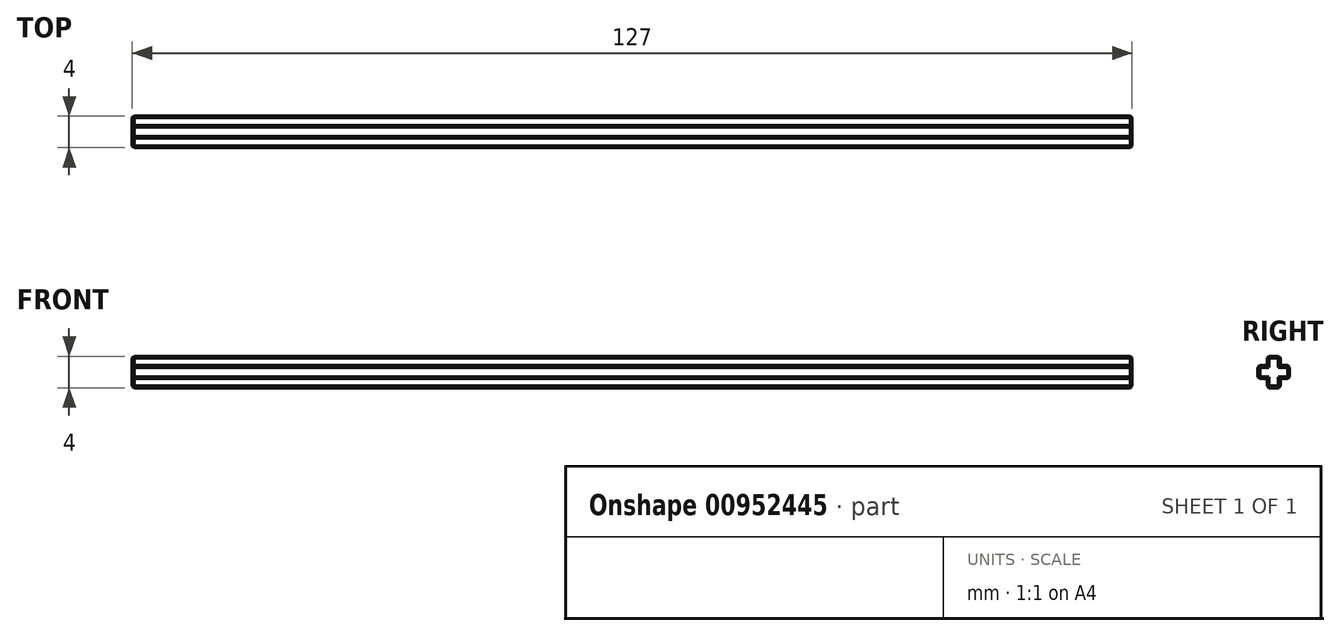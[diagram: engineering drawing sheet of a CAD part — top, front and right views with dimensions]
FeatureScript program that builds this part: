
annotation { "Feature Type Name" : "Feature", "Feature Type Description" : "" }
export const myFeature = defineFeature(function(context is Context, id is Id, definition is map)
    precondition{}
    {
        {
            var Q0;
            Q0=qCreatedBy(makeId("Right.planeOp"),FACE);
            var sketch = newSketch(context, id + "F0", { "sketchPlane" : qUnion([Q0])});
            skLineSegment(sketch, "E0.bottom", {"start": v(0.8, 2) * mm, "end": v(-0.8, 2) * mm});
            skLineSegment(sketch, "E0.top", {"start": v(0.8, -2) * mm, "end": v(-0.8, -2) * mm});
            skLineSegment(sketch, "E0.left", {"start": v(0.8, 2) * mm, "end": v(0.8, -2) * mm});
            skLineSegment(sketch, "E0.right", {"start": v(-0.8, 2) * mm, "end": v(-0.8, -2) * mm});
            skPoint(sketch, "E0.middle", {"position": v(0, 0) * mm});
            skLineSegment(sketch, "E1.bottom", {"start": v(-2, -0.8) * mm, "end": v(2, -0.8) * mm});
            skLineSegment(sketch, "E1.top", {"start": v(-2, 0.8) * mm, "end": v(2, 0.8) * mm});
            skLineSegment(sketch, "E1.left", {"start": v(-2, -0.8) * mm, "end": v(-2, 0.8) * mm});
            skLineSegment(sketch, "E1.right", {"start": v(2, -0.8) * mm, "end": v(2, 0.8) * mm});
            skSolve(sketch);
        }
        {
            var Q0;
            {var subQ5=sQuery(id+"F0.wireOp",EDGE,"E1.left");Q0=makeQuery(id+"F0.imprint","IMPRINT",FACE,{"disambiguationData":[TD([[makeQuery(id+"F0.imprint","IMPRINT",EDGE,{"derivedFrom":subQ5}),-1.0]])]});}
            var Q1;
            {var subQ0=sQuery(id+"F0.wireOp",EDGE,"E1.top");var subQ1=sQuery(id+"F0.wireOp",EDGE,"E0.left");var subQ2=makeQuery(id+"F0.imprint","INTERSECT",VERTEX,{"derivedFrom":[subQ1,subQ0]});Q1=makeQuery(id+"F0.imprint","IMPRINT",FACE,{"disambiguationData":[TD([[makeQuery(id+"F0.imprint","IMPRINT",EDGE,{"disambiguationData":[TD([[subQ2,-1.0]])],"derivedFrom":subQ1}),-1.0]])]});}
            var Q2;
            {var subQ0=sQuery(id+"F0.wireOp",EDGE,"E0.top");Q2=makeQuery(id+"F0.imprint","IMPRINT",FACE,{"disambiguationData":[TD([[makeQuery(id+"F0.imprint","IMPRINT",EDGE,{"derivedFrom":subQ0}),-1.0]])]});}
            var Q3;
            {var subQ5=sQuery(id+"F0.wireOp",EDGE,"E1.right");Q3=makeQuery(id+"F0.imprint","IMPRINT",FACE,{"disambiguationData":[TD([[makeQuery(id+"F0.imprint","IMPRINT",EDGE,{"derivedFrom":subQ5}),1.0]])]});}
            var Q4;
            {var subQ0=sQuery(id+"F0.wireOp",EDGE,"E0.bottom");Q4=makeQuery(id+"F0.imprint","IMPRINT",FACE,{"disambiguationData":[TD([[makeQuery(id+"F0.imprint","IMPRINT",EDGE,{"derivedFrom":subQ0}),1.0]])]});}
            extrude(context, id + "F1", {"entities" : qUnion([Q0, Q1, Q2, Q3, Q4]), "depth" : 127 * mm, "offsetDistance" : 25.4 * mm});
        }
        {
            var Q0;
            Q0=makeQuery(id+"F1.opExtrude","SWEPT_EDGE",EDGE,{"disambiguationData":[OSD([sQuery(id+"F0.wireOp",EDGE,"ookbRjFh-wDmi-CqYK-rmM9-PLN8MNht7uDI"),sQuery(id+"F0.wireOp",EDGE,"E1.bottom"),sQuery(id+"F0.wireOp",EDGE,"E1.left")])]});
            var Q1;
            Q1=makeQuery(id+"F1.opExtrude","SWEPT_EDGE",EDGE,{"disambiguationData":[OSD([sQuery(id+"F0.wireOp",EDGE,"ookbRjFh-wDmi-CqYK-rmM9-PLN8MNht7uDI"),sQuery(id+"F0.wireOp",EDGE,"E1.top"),sQuery(id+"F0.wireOp",EDGE,"E1.left")])]});
            var Q2;
            Q2=makeQuery(id+"F1.opExtrude","SWEPT_EDGE",EDGE,{"disambiguationData":[OSD([sQuery(id+"F0.wireOp",EDGE,"ookbRjFh-wDmi-CqYK-rmM9-PLN8MNht7uDI"),sQuery(id+"F0.wireOp",EDGE,"E0.bottom"),sQuery(id+"F0.wireOp",EDGE,"E0.right")])]});
            var Q3;
            Q3=makeQuery(id+"F1.opExtrude","SWEPT_EDGE",EDGE,{"disambiguationData":[OSD([sQuery(id+"F0.wireOp",EDGE,"ookbRjFh-wDmi-CqYK-rmM9-PLN8MNht7uDI"),sQuery(id+"F0.wireOp",EDGE,"E0.top"),sQuery(id+"F0.wireOp",EDGE,"E0.right")])]});
            var Q4;
            Q4=makeQuery(id+"F1.opExtrude","SWEPT_EDGE",EDGE,{"disambiguationData":[OSD([sQuery(id+"F0.wireOp",EDGE,"ookbRjFh-wDmi-CqYK-rmM9-PLN8MNht7uDI"),sQuery(id+"F0.wireOp",EDGE,"E0.top"),sQuery(id+"F0.wireOp",EDGE,"E0.left")])]});
            var Q5;
            Q5=makeQuery(id+"F1.opExtrude","SWEPT_EDGE",EDGE,{"disambiguationData":[OSD([sQuery(id+"F0.wireOp",EDGE,"ookbRjFh-wDmi-CqYK-rmM9-PLN8MNht7uDI"),sQuery(id+"F0.wireOp",EDGE,"E1.bottom"),sQuery(id+"F0.wireOp",EDGE,"E1.right")])]});
            var Q6;
            Q6=makeQuery(id+"F1.opExtrude","SWEPT_EDGE",EDGE,{"disambiguationData":[OSD([sQuery(id+"F0.wireOp",EDGE,"ookbRjFh-wDmi-CqYK-rmM9-PLN8MNht7uDI"),sQuery(id+"F0.wireOp",EDGE,"E1.top"),sQuery(id+"F0.wireOp",EDGE,"E1.right")])]});
            var Q7;
            Q7=makeQuery(id+"F1.opExtrude","SWEPT_EDGE",EDGE,{"disambiguationData":[OSD([sQuery(id+"F0.wireOp",EDGE,"ookbRjFh-wDmi-CqYK-rmM9-PLN8MNht7uDI"),sQuery(id+"F0.wireOp",EDGE,"E0.bottom"),sQuery(id+"F0.wireOp",EDGE,"E0.left")])]});
            var Q8;
            {var subQ0=sQuery(id+"F0.wireOp",EDGE,"E1.bottom");Q8=makeQuery(id+"F1.opExtrude","CAP_EDGE",EDGE,{"disambiguationData":[OSD([subQ0]),TDD([makeQuery(id+"F0.imprint","IMPRINT",EDGE,{"disambiguationData":[TD([[makeQuery(id+"F0.imprint","INTERSECT",VERTEX,{"derivedFrom":[sQuery(id+"F0.wireOp",EDGE,"E0.right"),subQ0]}),1.0]])],"derivedFrom":subQ0})])],"isStart":false});}
            var Q9;
            {var subQ0=sQuery(id+"F0.wireOp",EDGE,"E0.right");Q9=makeQuery(id+"F1.opExtrude","CAP_EDGE",EDGE,{"disambiguationData":[OSD([subQ0]),TDD([makeQuery(id+"F0.imprint","IMPRINT",EDGE,{"disambiguationData":[TD([[makeQuery(id+"F0.imprint","INTERSECT",VERTEX,{"derivedFrom":[subQ0,sQuery(id+"F0.wireOp",EDGE,"E1.bottom")]}),-1.0]])],"derivedFrom":subQ0})])],"isStart":false});}
            var Q10;
            Q10=makeQuery(id+"F1.opExtrude","CAP_EDGE",EDGE,{"disambiguationData":[OSD([sQuery(id+"F0.wireOp",EDGE,"E0.top")])],"isStart":false});
            var Q11;
            {var subQ0=sQuery(id+"F0.wireOp",EDGE,"E0.left");Q11=makeQuery(id+"F1.opExtrude","CAP_EDGE",EDGE,{"disambiguationData":[OSD([subQ0]),TDD([makeQuery(id+"F0.imprint","IMPRINT",EDGE,{"disambiguationData":[TD([[makeQuery(id+"F0.imprint","INTERSECT",VERTEX,{"derivedFrom":[subQ0,sQuery(id+"F0.wireOp",EDGE,"E1.bottom")]}),-1.0]])],"derivedFrom":subQ0})])],"isStart":false});}
            var Q12;
            {var subQ0=sQuery(id+"F0.wireOp",EDGE,"E1.bottom");Q12=makeQuery(id+"F1.opExtrude","CAP_EDGE",EDGE,{"disambiguationData":[OSD([subQ0]),TDD([makeQuery(id+"F0.imprint","IMPRINT",EDGE,{"disambiguationData":[TD([[makeQuery(id+"F0.imprint","INTERSECT",VERTEX,{"derivedFrom":[sQuery(id+"F0.wireOp",EDGE,"E0.left"),subQ0]}),-1.0]])],"derivedFrom":subQ0})])],"isStart":false});}
            var Q13;
            Q13=makeQuery(id+"F1.opExtrude","CAP_EDGE",EDGE,{"disambiguationData":[OSD([sQuery(id+"F0.wireOp",EDGE,"E1.right")])],"isStart":false});
            var Q14;
            {var subQ0=sQuery(id+"F0.wireOp",EDGE,"E1.top");Q14=makeQuery(id+"F1.opExtrude","CAP_EDGE",EDGE,{"disambiguationData":[OSD([subQ0]),TDD([makeQuery(id+"F0.imprint","IMPRINT",EDGE,{"disambiguationData":[TD([[makeQuery(id+"F0.imprint","INTERSECT",VERTEX,{"derivedFrom":[sQuery(id+"F0.wireOp",EDGE,"E0.left"),subQ0]}),-1.0]])],"derivedFrom":subQ0})])],"isStart":false});}
            var Q15;
            Q15=makeQuery(id+"F1.opExtrude","CAP_EDGE",EDGE,{"disambiguationData":[OSD([sQuery(id+"F0.wireOp",EDGE,"E0.bottom")])],"isStart":false});
            var Q16;
            {var subQ0=sQuery(id+"F0.wireOp",EDGE,"E0.right");Q16=makeQuery(id+"F1.opExtrude","CAP_EDGE",EDGE,{"disambiguationData":[OSD([subQ0]),TDD([makeQuery(id+"F0.imprint","IMPRINT",EDGE,{"disambiguationData":[TD([[makeQuery(id+"F0.imprint","INTERSECT",VERTEX,{"derivedFrom":[subQ0,sQuery(id+"F0.wireOp",EDGE,"E1.top")]}),1.0]])],"derivedFrom":subQ0})])],"isStart":false});}
            var Q17;
            {var subQ0=sQuery(id+"F0.wireOp",EDGE,"E0.left");Q17=makeQuery(id+"F1.opExtrude","CAP_EDGE",EDGE,{"disambiguationData":[OSD([subQ0]),TDD([makeQuery(id+"F0.imprint","IMPRINT",EDGE,{"disambiguationData":[TD([[makeQuery(id+"F0.imprint","INTERSECT",VERTEX,{"derivedFrom":[subQ0,sQuery(id+"F0.wireOp",EDGE,"E1.top")]}),1.0]])],"derivedFrom":subQ0})])],"isStart":false});}
            var Q18;
            Q18=makeQuery(id+"F1.opExtrude","CAP_EDGE",EDGE,{"disambiguationData":[OSD([sQuery(id+"F0.wireOp",EDGE,"E1.left")])],"isStart":false});
            var Q19;
            Q19=makeQuery(id+"F1.opExtrude","CAP_EDGE",EDGE,{"disambiguationData":[OSD([sQuery(id+"F0.wireOp",EDGE,"E1.left")])],"isStart":true});
            var Q20;
            {var subQ0=sQuery(id+"F0.wireOp",EDGE,"E1.top");Q20=makeQuery(id+"F1.opExtrude","CAP_EDGE",EDGE,{"disambiguationData":[OSD([subQ0]),TDD([makeQuery(id+"F0.imprint","IMPRINT",EDGE,{"disambiguationData":[TD([[makeQuery(id+"F0.imprint","INTERSECT",VERTEX,{"derivedFrom":[sQuery(id+"F0.wireOp",EDGE,"E0.right"),subQ0]}),1.0]])],"derivedFrom":subQ0})])],"isStart":true});}
            var Q21;
            {var subQ0=sQuery(id+"F0.wireOp",EDGE,"E0.right");Q21=makeQuery(id+"F1.opExtrude","CAP_EDGE",EDGE,{"disambiguationData":[OSD([subQ0]),TDD([makeQuery(id+"F0.imprint","IMPRINT",EDGE,{"disambiguationData":[TD([[makeQuery(id+"F0.imprint","INTERSECT",VERTEX,{"derivedFrom":[subQ0,sQuery(id+"F0.wireOp",EDGE,"E1.top")]}),1.0]])],"derivedFrom":subQ0})])],"isStart":true});}
            var Q22;
            Q22=makeQuery(id+"F1.opExtrude","CAP_EDGE",EDGE,{"disambiguationData":[OSD([sQuery(id+"F0.wireOp",EDGE,"E0.bottom")])],"isStart":true});
            var Q23;
            {var subQ0=sQuery(id+"F0.wireOp",EDGE,"E0.right");Q23=makeQuery(id+"F1.opExtrude","CAP_EDGE",EDGE,{"disambiguationData":[OSD([subQ0]),TDD([makeQuery(id+"F0.imprint","IMPRINT",EDGE,{"disambiguationData":[TD([[makeQuery(id+"F0.imprint","INTERSECT",VERTEX,{"derivedFrom":[subQ0,sQuery(id+"F0.wireOp",EDGE,"E1.bottom")]}),-1.0]])],"derivedFrom":subQ0})])],"isStart":true});}
            var Q24;
            Q24=makeQuery(id+"F1.opExtrude","CAP_EDGE",EDGE,{"disambiguationData":[OSD([sQuery(id+"F0.wireOp",EDGE,"E0.top")])],"isStart":true});
            var Q25;
            {var subQ0=sQuery(id+"F0.wireOp",EDGE,"E0.left");Q25=makeQuery(id+"F1.opExtrude","CAP_EDGE",EDGE,{"disambiguationData":[OSD([subQ0]),TDD([makeQuery(id+"F0.imprint","IMPRINT",EDGE,{"disambiguationData":[TD([[makeQuery(id+"F0.imprint","INTERSECT",VERTEX,{"derivedFrom":[subQ0,sQuery(id+"F0.wireOp",EDGE,"E1.bottom")]}),-1.0]])],"derivedFrom":subQ0})])],"isStart":true});}
            var Q26;
            {var subQ0=sQuery(id+"F0.wireOp",EDGE,"E1.bottom");Q26=makeQuery(id+"F1.opExtrude","CAP_EDGE",EDGE,{"disambiguationData":[OSD([subQ0]),TDD([makeQuery(id+"F0.imprint","IMPRINT",EDGE,{"disambiguationData":[TD([[makeQuery(id+"F0.imprint","INTERSECT",VERTEX,{"derivedFrom":[sQuery(id+"F0.wireOp",EDGE,"E0.left"),subQ0]}),-1.0]])],"derivedFrom":subQ0})])],"isStart":true});}
            var Q27;
            Q27=makeQuery(id+"F1.opExtrude","CAP_EDGE",EDGE,{"disambiguationData":[OSD([sQuery(id+"F0.wireOp",EDGE,"E1.right")])],"isStart":true});
            var Q28;
            {var subQ0=sQuery(id+"F0.wireOp",EDGE,"E1.top");Q28=makeQuery(id+"F1.opExtrude","CAP_EDGE",EDGE,{"disambiguationData":[OSD([subQ0]),TDD([makeQuery(id+"F0.imprint","IMPRINT",EDGE,{"disambiguationData":[TD([[makeQuery(id+"F0.imprint","INTERSECT",VERTEX,{"derivedFrom":[sQuery(id+"F0.wireOp",EDGE,"E0.left"),subQ0]}),-1.0]])],"derivedFrom":subQ0})])],"isStart":true});}
            var Q29;
            {var subQ0=sQuery(id+"F0.wireOp",EDGE,"E0.left");Q29=makeQuery(id+"F1.opExtrude","CAP_EDGE",EDGE,{"disambiguationData":[OSD([subQ0]),TDD([makeQuery(id+"F0.imprint","IMPRINT",EDGE,{"disambiguationData":[TD([[makeQuery(id+"F0.imprint","INTERSECT",VERTEX,{"derivedFrom":[subQ0,sQuery(id+"F0.wireOp",EDGE,"E1.top")]}),1.0]])],"derivedFrom":subQ0})])],"isStart":true});}
            var Q30;
            {var subQ0=sQuery(id+"F0.wireOp",EDGE,"E1.top");Q30=makeQuery(id+"F1.opExtrude","CAP_EDGE",EDGE,{"disambiguationData":[OSD([subQ0]),TDD([makeQuery(id+"F0.imprint","IMPRINT",EDGE,{"disambiguationData":[TD([[makeQuery(id+"F0.imprint","INTERSECT",VERTEX,{"derivedFrom":[subQ0,sQuery(id+"F0.wireOp",EDGE,"E1.left")]}),-1.0]])],"derivedFrom":subQ0})])],"isStart":false});}
            var Q31;
            {var subQ0=sQuery(id+"F0.wireOp",EDGE,"E1.bottom");Q31=makeQuery(id+"F1.opExtrude","CAP_EDGE",EDGE,{"disambiguationData":[OSD([subQ0]),TDD([makeQuery(id+"F0.imprint","IMPRINT",EDGE,{"disambiguationData":[TD([[makeQuery(id+"F0.imprint","INTERSECT",VERTEX,{"derivedFrom":[subQ0,sQuery(id+"F0.wireOp",EDGE,"E1.left")]}),-1.0]])],"derivedFrom":subQ0})])],"isStart":true});}
            chamfer(context, id + "F2", {"entities" : qUnion([Q0, Q1, Q2, Q3, Q4, Q5, Q6, Q7, Q8, Q9, Q10, Q11, Q12, Q13, Q14, Q15, Q16, Q17, Q18, Q19, Q20, Q21, Q22, Q23, Q24, Q25, Q26, Q27, Q28, Q29, Q30, Q31]), "width" : 0.2 * mm, "tangentPropagation" : true});
        }
    });
